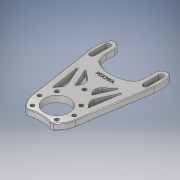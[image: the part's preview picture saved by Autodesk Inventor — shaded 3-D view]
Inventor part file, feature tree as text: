
AUTODESK INVENTOR PART (.ipt)
format: ipt  version: 2019.3 (Build 233278000, 278)  size: 677,888 bytes
history: native  units: mm
features: thread x7, emboss x2, fillet x2, sketch x2, extrude x1, chamfer x1, other x1
ambient origin geometry x8: Origin, YZ Plane, XZ Plane, XY Plane, X Axis, Y Axis, Z Axis, Center Point
bodies: Body1 (feature_tree)
feature tree (16):
  extrude  "Extrusion3"  Depth=20.0mm
  thread  "Thread1"  [1 undecoded]
  thread  "Thread2"  [1 undecoded]
  thread  "Thread3"  [1 undecoded]
  thread  "Thread4"  [1 undecoded]
  thread  "Thread5"  [1 undecoded]
  thread  "Thread6"  [1 undecoded]
  thread  "Thread7"  [1 undecoded]
  emboss  "Emboss1"
  emboss  "Emboss2"
  fillet  "Fillet3"  Radius=3.0mm
  fillet  "Fillet5"  Radius=3.0mm
  chamfer  "Chamfer3"  Angle=45.0deg  [1 undecoded]
  other  "Center Lines"
  sketch  "Sketch1"  dims[d0=55.6mm d1=20.0mm d3=3.5mm d4=3.5mm d5=7.0mm d7=43.0mm d9=3.5mm d11=32.0mm d15=4.0mm d24=3.0mm d25=3.0mm]
  sketch  "Sketch3"  dims[d26=90.0deg d27=45.0deg d29=3.0mm d30=3.0mm d31=22.0mm d40=5.0mm d41=0.0mm d44=10.0mm d45=0.0mm d46=10.0mm d47=0.0mm d48=10.0mm d49=0.0mm d50=20.0mm d51=52.0mm d53=26.0mm d54=10.0mm d55=0.0mm d56=10.0mm d57=0.0mm d58=10.0mm d59=0.0mm d60=10.0mm d61=0.0mm d65=0.2mm d66=0.0mm d67=14.0mm d68=14.0mm d69=5.0mm d70=15.0mm d71=5.0mm d72=15.0mm d73=0.2mm d74=0.0mm d75=84.563203mm d76=7.5mm d77=3.75mm d78=1.0mm d81=6.25mm d82=12.5mm d85=5.0mm d86=4.0mm d87=8.0mm d91=0.5mm d93=4.2mm d94=2.0mm d95=0.5mm d96=2.0mm d97=45.0deg d98=15.0deg d99=24.0mm]
note: 8 required parameter values undecoded (feature->parameter linkage not recoverable at this tier; creation-order binding heuristic only, values carry confidence <= 0.55)
